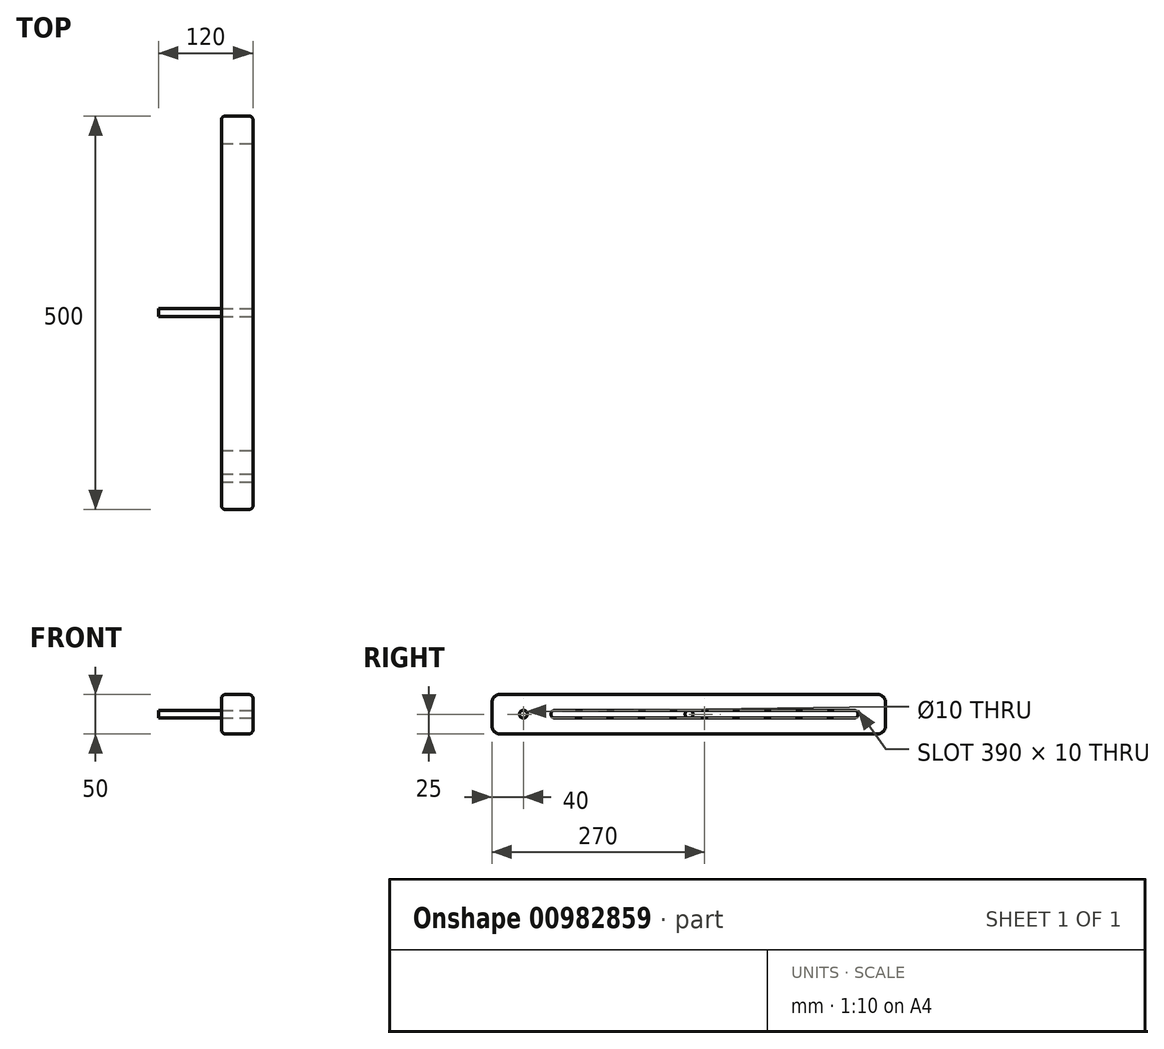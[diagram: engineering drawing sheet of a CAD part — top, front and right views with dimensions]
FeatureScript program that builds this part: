
annotation { "Feature Type Name" : "Feature", "Feature Type Description" : "" }
export const myFeature = defineFeature(function(context is Context, id is Id, definition is map)
    precondition{}
    {
        {
            var Q0;
            Q0=qCreatedBy(makeId("Right.planeOp"),FACE);
            var sketch = newSketch(context, id + "F0", { "sketchPlane" : qUnion([Q0])});
            skLineSegment(sketch, "E0.bottom", {"start": v(250, 25) * mm, "end": v(-250, 25) * mm});
            skLineSegment(sketch, "E0.top", {"start": v(250, -25) * mm, "end": v(-250, -25) * mm});
            skLineSegment(sketch, "E0.left", {"start": v(250, 25) * mm, "end": v(250, -25) * mm});
            skLineSegment(sketch, "E0.right", {"start": v(-250, 25) * mm, "end": v(-250, -25) * mm});
            skPoint(sketch, "E0.middle", {"position": v(0, 0) * mm});
            skPoint(sketch, "E1", {"position": v(-210, 0) * mm});
            skCircle(sketch, "E2", {"center": v(-210, 0) * mm, "radius": 5 * mm});
            skLineSegment(sketch, "E3", {"start": v(-170, 0) * mm, "end": v(210, 0) * mm});
            skArc(sketch, "E4.0.startCap", {"start": v(-170, -5) * mm, "mid": v(-175, 0) * mm, "end": v(-170, 5) * mm});
            skArc(sketch, "E4.0.endCap", {"start": v(210, 5) * mm, "mid": v(215, 0) * mm, "end": v(210, -5) * mm});
            skLineSegment(sketch, "E4.0.left", {"start": v(-170, 5) * mm, "end": v(210, 5) * mm});
            skLineSegment(sketch, "E4.0.right", {"start": v(-170, -5) * mm, "end": v(210, -5) * mm});
            skSolve(sketch);
        }
        {
            var Q0;
            Q0=makeQuery(id+"F0.imprint","IMPRINT",FACE,{"disambiguationData":[TD([[makeQuery(id+"F0.imprint","IMPRINT",EDGE,{"derivedFrom":sQuery(id+"F0.wireOp",EDGE,"E0.bottom")}),1.0]])]});
            extrude(context, id + "F1", {"entities" : qUnion([Q0]), "oppositeDirection" : true, "depth" : 40 * mm, "offsetDistance" : 25 * mm});
        }
        {
            var Q0;
            Q0=makeQuery(id+"F1.opExtrude","SWEPT_EDGE",EDGE,{"disambiguationData":[OSD([sQuery(id+"F0.wireOp",EDGE,"E0.bottom"),sQuery(id+"F0.wireOp",EDGE,"E0.right")])]});
            var Q1;
            Q1=makeQuery(id+"F1.opExtrude","SWEPT_EDGE",EDGE,{"disambiguationData":[OSD([sQuery(id+"F0.wireOp",EDGE,"E0.top"),sQuery(id+"F0.wireOp",EDGE,"E0.right")])]});
            var Q2;
            Q2=makeQuery(id+"F1.opExtrude","SWEPT_EDGE",EDGE,{"disambiguationData":[OSD([sQuery(id+"F0.wireOp",EDGE,"E0.bottom"),sQuery(id+"F0.wireOp",EDGE,"E0.left")])]});
            var Q3;
            Q3=makeQuery(id+"F1.opExtrude","SWEPT_EDGE",EDGE,{"disambiguationData":[OSD([sQuery(id+"F0.wireOp",EDGE,"E0.top"),sQuery(id+"F0.wireOp",EDGE,"E0.left")])]});
            fillet(context, id + "F2", {"entities" : qUnion([Q0, Q1, Q2, Q3]), "radius" : 10 * mm, "tangentPropagation" : true, "allowEdgeOverflow" : false});
        }
        {
            var Q0;
            Q0=makeQuery(id+"F1.opExtrude","CAP_EDGE",EDGE,{"disambiguationData":[OSD([sQuery(id+"F0.wireOp",EDGE,"E0.bottom")])],"isStart":true});
            var Q1;
            Q1=makeQuery(id+"F1.opExtrude","CAP_EDGE",EDGE,{"disambiguationData":[OSD([sQuery(id+"F0.wireOp",EDGE,"E0.bottom")])],"isStart":false});
            fillet(context, id + "F3", {"entities" : qUnion([Q0, Q1]), "radius" : 5 * mm, "tangentPropagation" : true, "allowEdgeOverflow" : false});
        }
        {
            var Q0;
            Q0=qCreatedBy(makeId("Right.planeOp"),FACE);
            var sketch = newSketch(context, id + "F4", { "sketchPlane" : qUnion([Q0])});
            skCircle(sketch, "E5", {"center": v(0.35, 0) * mm, "radius": 5 * mm});
            skSolve(sketch);
        }
        {
            var Q0;
            Q0=makeQuery(id+"F4.imprint","IMPRINT",FACE,{"disambiguationData":[TD([[makeQuery(id+"F4.imprint","IMPRINT",EDGE,{"derivedFrom":sQuery(id+"F4.wireOp",EDGE,"E5")}),1.0]])]});
            extrude(context, id + "F5", {"entities" : qUnion([Q0]), "oppositeDirection" : true, "depth" : 120 * mm, "offsetDistance" : 25 * mm});
        }
    });
